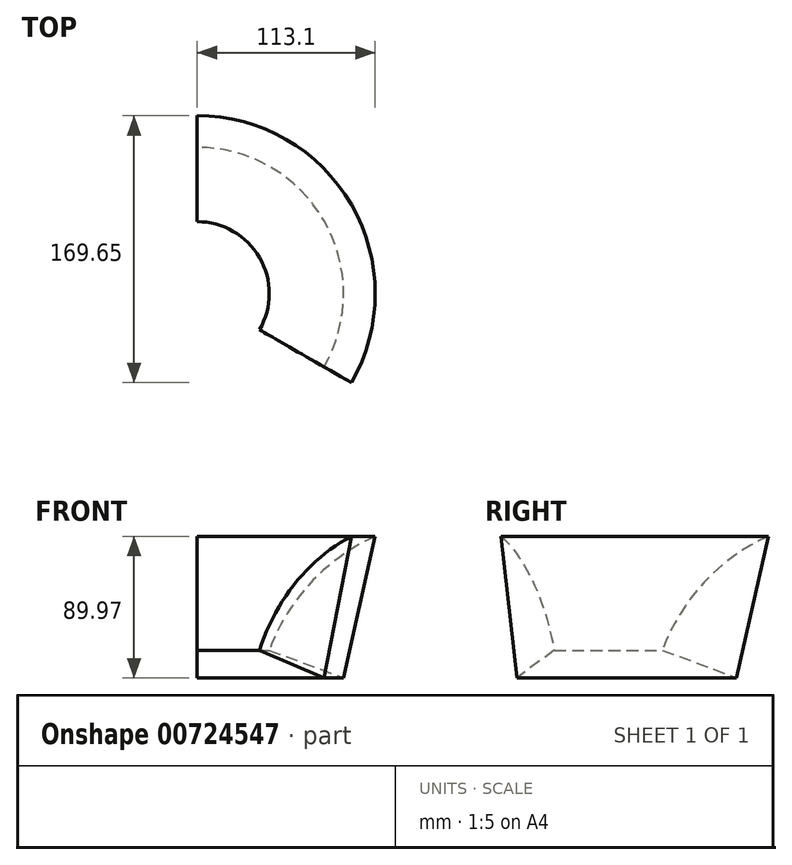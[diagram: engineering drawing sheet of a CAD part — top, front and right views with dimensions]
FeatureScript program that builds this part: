
annotation { "Feature Type Name" : "Feature", "Feature Type Description" : "" }
export const myFeature = defineFeature(function(context is Context, id is Id, definition is map)
    precondition{}
    {
        {
            var Q0;
            Q0=qCreatedBy(makeId("Front.planeOp"),FACE);
            var sketch = newSketch(context, id + "F0", { "sketchPlane" : qUnion([Q0])});
            skLineSegment(sketch, "E0", {"start": v(45.76, -178.62) * mm, "end": v(92.97, -196.21) * mm});
            skLineSegment(sketch, "E1", {"start": v(92.97, -196.21) * mm, "end": v(138.76, 8.46) * mm});
            skLineSegment(sketch, "E2", {"start": v(138.76, -97.63) * mm, "end": v(138.76, 8.46) * mm});
            skArc(sketch, "E3", {"start": v(138.76, -97.63) * mm, "mid": v(81.97, -126.31) * mm, "end": v(45.76, -178.62) * mm});
            skSolve(sketch);
        }
        {
            var Q0;
            Q0=qCreatedBy(makeId("Front.planeOp"),FACE);
            var sketch = newSketch(context, id + "F1", { "sketchPlane" : qUnion([Q0])});
            skLineSegment(sketch, "E4", {"start": v(0, 60.51) * mm, "end": v(0, -53.79) * mm});
            skSolve(sketch);
        }
        {
            var Q0;
            Q0=makeQuery(id+"F0.imprint","IMPRINT",FACE,{"disambiguationData":[TD([[makeQuery(id+"F0.imprint","IMPRINT",EDGE,{"derivedFrom":sQuery(id+"F0.wireOp",EDGE,"E0")}),1.0]])]});
            var Q1;
            Q1=sQuery(id+"F1.wireOp",EDGE,"E4");
            revolve(context, id + "F2", {"surfaceOperationType" : NewSurfaceOperationType.NEW, "entities" : qUnion([Q0]), "axis" : qUnion([Q1]), "revolveType" : RevolveType.TWO_DIRECTIONS, "angle" : 30 * degree, "angleBack" : 270 * degree});
        }
    });
